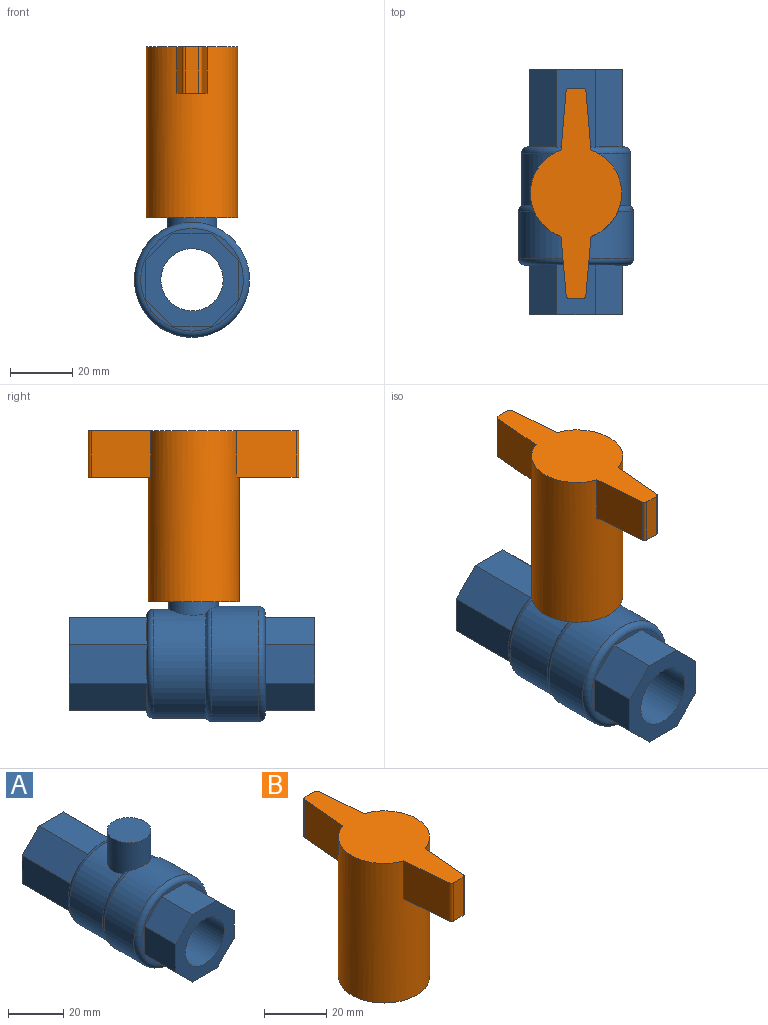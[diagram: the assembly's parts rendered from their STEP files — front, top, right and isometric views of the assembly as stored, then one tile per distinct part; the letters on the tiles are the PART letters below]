
ASSEMBLY  parts=2 mates=1
PART A: 35 faces, bbox 40.2x79.1x50.1 mm
  f0: plane 7.81x0.5mm, normal (0,1,0), area 2.6mm2, adj f18,f34
  f1: plane 5.52x5.52mm, normal (0,1,0), area 2.6mm2, adj f17,f34
  f2: plane 7.81x0.5mm, normal (0,1,0), area 2.6mm2, adj f16,f34
  f3: plane 5.52x5.52mm, normal (0,1,0), area 2.6mm2, adj f15,f34
  f4: plane 7.81x0.5mm, normal (0,1,0), area 2.6mm2, adj f14,f34
  f5: plane 5.52x5.52mm, normal (0,1,0), area 2.6mm2, adj f13,f34
  f6: plane 7.81x0.5mm, normal (0,1,0), area 2.6mm2, adj f12,f34
  f7: cylinder r=10mm len=79mm, axis (0,1,0), area 4963.7mm2, adj f19,f29
  f8: cylinder r=17.5mm len=35mm, axis (0,1,0), area 1703.8mm2, adj f31,f32,f34
  f9: cylinder r=18.5mm len=37mm, axis (0,1,0), area 1757.2mm2, adj f31,f32,f33
  f10: plane 33x33mm, normal (0,-1,0), area 109.7mm2, adj f21,f22,f23,f24,f25,f26,f27,f28
  f11: plane 25.24x8.89mm, normal (-0.71,0,0.71), area 310.9mm2, adj f12,f18,f19,f20,f34
  f12: plane 25.24x12.53mm, normal (-1,0,0), area 310.9mm2, adj f6,f11,f13,f19,f34
  f13: plane 25.24x8.89mm, normal (-0.71,0,-0.71), area 310.9mm2, adj f5,f12,f14,f19,f34
  f14: plane 25.24x12.53mm, normal (0,0,-1), area 310.9mm2, adj f4,f13,f15,f19,f34
  f15: plane 25.24x8.89mm, normal (0.71,0,-0.71), area 310.9mm2, adj f3,f14,f16,f19,f34
  f16: plane 25.24x12.53mm, normal (1,0,0), area 310.9mm2, adj f2,f15,f17,f19,f34
  f17: plane 25.24x8.89mm, normal (0.71,0,0.71), area 310.9mm2, adj f1,f16,f18,f19,f34
  f18: plane 25.24x12.53mm, normal (0,0,1), area 310.9mm2, adj f0,f11,f17,f19,f34
  f19: plane 30x30mm, normal (0,1,0), area 431.4mm2, adj f7,f11,f12,f13,f14,f15,f16,f17
  f20: plane 5.52x5.52mm, normal (0,1,0), area 2.6mm2, adj f11,f34
  f21: plane 16x8.79mm, normal (-0.71,0,0.71), area 198.8mm2, adj f10,f22,f28,f29
  f22: plane 16x12.43mm, normal (-1,0,0), area 198.8mm2, adj f10,f21,f23,f29
  f23: plane 16x8.79mm, normal (-0.71,0,-0.71), area 198.8mm2, adj f10,f22,f24,f29
  f24: plane 16x12.43mm, normal (0,0,-1), area 198.8mm2, adj f10,f23,f25,f29
  f25: plane 16x8.79mm, normal (0.71,0,-0.71), area 198.8mm2, adj f10,f24,f26,f29
  f26: plane 16x12.43mm, normal (1,0,0), area 198.8mm2, adj f10,f25,f27,f29
  f27: plane 16x8.79mm, normal (0.71,0,0.71), area 198.8mm2, adj f10,f26,f28,f29
  f28: plane 16x12.43mm, normal (0,0,1), area 198.8mm2, adj f10,f21,f27,f29
  f29: plane 30x30mm, normal (0,-1,0), area 431.4mm2, adj f7,f21,f22,f23,f24,f25,f26,f27
  f30: plane 15.95x15.95mm, normal (0,0,1), area 199.7mm2, adj f31
  f31: cylinder r=7.97mm len=15.95mm, axis (0,0,-1), area 657.7mm2, adj f8,f9,f30,f32
  f32: torus R=16.5mm, axis (0,1,0), area 211.9mm2, adj f8,f9,f31
  f33: torus R=16.5mm, axis (0,-1,0), area 350.8mm2, adj f9,f10
  f34: torus R=15.5mm, axis (0,-1,0), area 318mm2, adj f0,f1,f2,f3,f4,f5,f6,f8
PART B: 17 faces, bbox 29.3x67.7x55 mm
  f0: cylinder r=7.97mm len=15.95mm, axis (0,0,1), area 501mm2, adj f2,f3
  f1: cylinder r=14.67mm len=55mm, axis (0,0,1), area 4774.4mm2, adj f2,f4,f5,f9,f10,f11,f15,f16
  f2: plane 29.34x29.34mm, normal (0,0,-1), area 476.5mm2, adj f0,f1
  f3: plane 15.95x15.95mm, normal (0,0,-1), area 199.7mm2, adj f0
  f4: plane 67.7x29.34mm, normal (0,0,1), area 981.9mm2, adj f1,f5,f6,f7,f8,f9,f11,f12
  f5: plane 19.09x15mm, normal (1,0.09,0), area 287.4mm2, adj f1,f4,f6,f10
  f6: cylinder r=1mm len=15mm, axis (0,0,1), area 22.3mm2, adj f4,f5,f7,f10
  f7: plane 15x4.34mm, normal (0,1,0), area 65.1mm2, adj f4,f6,f8,f10
  f8: cylinder r=1mm len=15mm, axis (0,0,1), area 22.3mm2, adj f4,f7,f9,f10
  f9: plane 19.09x15mm, normal (-1,0.09,0), area 287.4mm2, adj f1,f4,f8,f10
  f10: plane 20x9.67mm, normal (0,0,-1), area 152.8mm2, adj f1,f5,f6,f7,f8,f9
  f11: plane 19.09x15mm, normal (-1,-0.09,0), area 287.4mm2, adj f1,f4,f12,f16
  f12: cylinder r=1mm len=15mm, axis (0,0,1), area 22.3mm2, adj f4,f11,f13,f16
  f13: plane 15x4.34mm, normal (0,-1,0), area 65.1mm2, adj f4,f12,f14,f16
  f14: cylinder r=1mm len=15mm, axis (0,0,1), area 22.3mm2, adj f4,f13,f15,f16
  f15: plane 19.09x15mm, normal (1,-0.09,0), area 287.4mm2, adj f1,f4,f14,f16
  f16: plane 20x9.67mm, normal (0,0,-1), area 152.8mm2, adj f1,f11,f12,f13,f14,f15
PLACE A at identity
PLACE B at identity
MATE fastened B.f0 <-> A.f31  axis (0,0,-1) through (0,-40.03,30)mm
